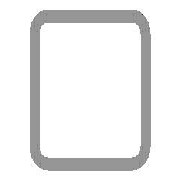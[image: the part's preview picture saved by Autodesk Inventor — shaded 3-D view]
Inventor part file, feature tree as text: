
AUTODESK INVENTOR PART (.ipt)
format: ipt  version: 2022 (Build 260153000, 153)  size: 249,856 bytes
history: native  units: mm (DEFAULTED — no unit token found)
features: other x7, sketch x3, surface_op x2, plane x1
ambient origin geometry x8: Origin, YZ Plane, XZ Plane, XY Plane, X Axis, Y Axis, Z Axis, Center Point
bodies: Solid1 (feature_tree), Body (feature_tree), Solid3 (feature_tree)
feature tree (13):
  parser-record x1  (decoder bookkeeping rows leaked as tree rows — omitted from the tree; the rows remain in map.json)
  other  "Driven Length"
  other  "Start Plane"
  other  "End Plane"
  sketch  "Sketch"  dims[d7=7.5mm d10=40.0mm d11=40.0mm d12=5.0mm d13=12.5mm d14=167.5mm d15=20.0mm d16=20.0mm d17=90.0deg d18=155.0mm d37=5.0mm d38=5.0mm d39=5.0mm d40=5.0mm d41=5.0mm d42=5.0mm d43=5.0mm d44=5.0mm d45=0.0mm d46=5.0mm d47=5.0mm d48=5.0mm d49=5.0mm d50=5.0mm d51=5.0mm d52=5.0mm d53=5.0mm d54=0.0mm]
  sketch  "Sketch3"  dims[d3=155.0mm]
  plane  "Work Plane3"
  sketch  "Sketch4"  dims[d4=0.0mm]
  other  "Srf5"
  other  "Srf6"
  other  "Srf4"
  surface_op  "Boundary Patch3"
  surface_op  "Boundary Patch4"
